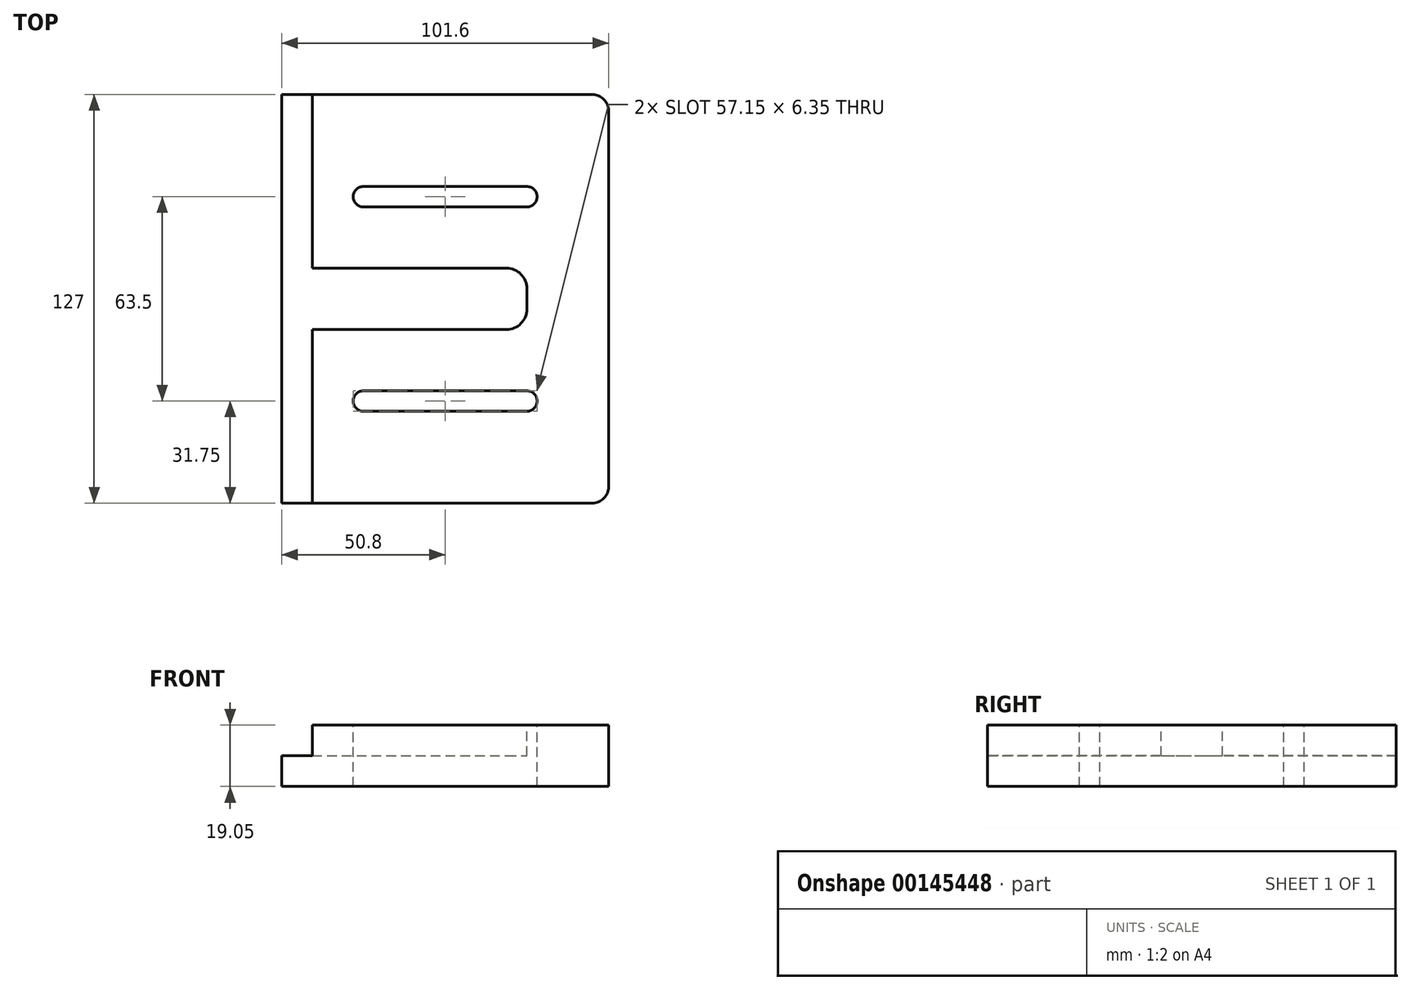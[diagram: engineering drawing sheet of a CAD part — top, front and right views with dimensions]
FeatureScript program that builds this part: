
annotation { "Feature Type Name" : "Feature", "Feature Type Description" : "" }
export const myFeature = defineFeature(function(context is Context, id is Id, definition is map)
    precondition{}
    {
        {
            var Q0;
            Q0=qCreatedBy(makeId("Top.planeOp"),FACE);
            var sketch = newSketch(context, id + "F0", { "sketchPlane" : qUnion([Q0])});
            skLineSegment(sketch, "E0.bottom", {"start": v(0, 0) * mm, "end": v(101.6, 0) * mm});
            skLineSegment(sketch, "E0.top", {"start": v(0, 127) * mm, "end": v(101.6, 127) * mm});
            skLineSegment(sketch, "E0.left", {"start": v(0, 0) * mm, "end": v(0, 127) * mm});
            skLineSegment(sketch, "E0.right", {"start": v(101.6, 0) * mm, "end": v(101.6, 127) * mm});
            skSolve(sketch);
        }
        {
            var Q0;
            Q0=makeQuery(id+"F0.imprint","IMPRINT",FACE,{"disambiguationData":[TD([[makeQuery(id+"F0.imprint","IMPRINT",EDGE,{"derivedFrom":sQuery(id+"F0.wireOp",EDGE,"E0.bottom")}),1.0]])]});
            extrude(context, id + "F1", {"entities" : qUnion([Q0]), "depth" : 19.05 * mm});
        }
        {
            var Q0;
            Q0=makeQuery(id+"F1.opExtrude","CAP_FACE",FACE,{"disambiguationData":[OSD([sQuery(id+"F0.wireOp",EDGE,"E0.bottom"),sQuery(id+"F0.wireOp",EDGE,"E0.top"),sQuery(id+"F0.wireOp",EDGE,"E0.left"),sQuery(id+"F0.wireOp",EDGE,"E0.right")])],"isStart":false});
            var sketch = newSketch(context, id + "F2", { "sketchPlane" : qUnion([Q0])});
            skLineSegment(sketch, "E1.bottom", {"start": v(0, 53.97) * mm, "end": v(76.2, 53.97) * mm});
            skLineSegment(sketch, "E1.top", {"start": v(0, 73.03) * mm, "end": v(76.2, 73.03) * mm});
            skLineSegment(sketch, "E1.left", {"start": v(0, 53.97) * mm, "end": v(0, 73.02) * mm});
            skLineSegment(sketch, "E1.right", {"start": v(76.2, 53.98) * mm, "end": v(76.2, 73.02) * mm});
            skLineSegment(sketch, "E2", {"start": v(76.2, 63.5) * mm, "end": v(0, 63.5) * mm, "construction": true});
            skSolve(sketch);
        }
        {
            var Q0;
            Q0 = qSketchRegion(id + "F2", true);
            extrude(context, id + "F3", {"entities" : qUnion([Q0]), "operationType" : NewBodyOperationType.REMOVE, "oppositeDirection" : true, "depth" : 9.52 * mm});
        }
        {
            var Q0;
            Q0=makeQuery(id+"F3.boolean.opBoolean","COPY",EDGE,{"derivedFrom":makeQuery(id+"F3.opExtrude","SWEPT_EDGE",EDGE,{"disambiguationData":[OSD([sQuery(id+"F2.wireOp",EDGE,"E1.top"),sQuery(id+"F2.wireOp",EDGE,"E1.right")])]})});
            var Q1;
            Q1=makeQuery(id+"F3.boolean.opBoolean","COPY",EDGE,{"derivedFrom":makeQuery(id+"F3.opExtrude","SWEPT_EDGE",EDGE,{"disambiguationData":[OSD([sQuery(id+"F2.wireOp",EDGE,"E1.bottom"),sQuery(id+"F2.wireOp",EDGE,"E1.right")])]})});
            fillet(context, id + "F4", {"entities" : qUnion([Q0, Q1]), "radius" : 6.35 * mm, "tangentPropagation" : true, "allowEdgeOverflow" : false});
        }
        {
            var Q0;
            Q0=makeQuery(id+"F1.opExtrude","CAP_FACE",FACE,{"disambiguationData":[OSD([sQuery(id+"F0.wireOp",EDGE,"E0.bottom"),sQuery(id+"F0.wireOp",EDGE,"E0.top"),sQuery(id+"F0.wireOp",EDGE,"E0.left"),sQuery(id+"F0.wireOp",EDGE,"E0.right")])],"isStart":false});
            var sketch = newSketch(context, id + "F5", { "sketchPlane" : qUnion([Q0])});
            skLineSegment(sketch, "E3", {"start": v(101.6, 63.5) * mm, "end": v(0, 63.5) * mm, "construction": true});
            skLineSegment(sketch, "E4", {"start": v(50.8, 63.5) * mm, "end": v(50.8, 0) * mm, "construction": true});
            skLineSegment(sketch, "E5", {"start": v(25.4, 31.75) * mm, "end": v(76.2, 31.75) * mm});
            skPoint(sketch, "E5.startSnap0", {"position": v(50.8, 31.75) * mm});
            skLineSegment(sketch, "E6.MirrorCS", {"start": v(25.4, 95.25) * mm, "end": v(76.2, 95.25) * mm});
            skArc(sketch, "E7.0.startCap", {"start": v(25.4, 28.58) * mm, "mid": v(22.22, 31.75) * mm, "end": v(25.4, 34.93) * mm});
            skArc(sketch, "E7.0.endCap", {"start": v(76.2, 34.93) * mm, "mid": v(79.37, 31.75) * mm, "end": v(76.2, 28.58) * mm});
            skLineSegment(sketch, "E7.0.left", {"start": v(25.4, 34.93) * mm, "end": v(76.2, 34.93) * mm});
            skLineSegment(sketch, "E7.0.right", {"start": v(25.4, 28.58) * mm, "end": v(76.2, 28.58) * mm});
            skArc(sketch, "E8.0.startCap", {"start": v(25.4, 92.08) * mm, "mid": v(22.23, 95.25) * mm, "end": v(25.4, 98.43) * mm});
            skArc(sketch, "E8.0.endCap", {"start": v(76.2, 98.43) * mm, "mid": v(79.37, 95.25) * mm, "end": v(76.2, 92.08) * mm});
            skLineSegment(sketch, "E8.0.left", {"start": v(25.4, 98.43) * mm, "end": v(76.2, 98.43) * mm});
            skLineSegment(sketch, "E8.0.right", {"start": v(25.4, 92.08) * mm, "end": v(76.2, 92.08) * mm});
            skSolve(sketch);
        }
        {
            var Q0;
            Q0 = qSketchRegion(id + "F5", true);
            extrude(context, id + "F6", {"entities" : qUnion([Q0]), "operationType" : NewBodyOperationType.REMOVE, "endBound" : BoundingType.THROUGH_ALL, "oppositeDirection" : true, "depth" : 25.4 * mm});
        }
        {
            var Q0;
            Q0=makeQuery(id+"F1.opExtrude","SWEPT_EDGE",EDGE,{"disambiguationData":[OSD([sQuery(id+"F0.wireOp",EDGE,"E0.bottom"),sQuery(id+"F0.wireOp",EDGE,"E0.right")])]});
            var Q1;
            Q1=makeQuery(id+"F1.opExtrude","SWEPT_EDGE",EDGE,{"disambiguationData":[OSD([sQuery(id+"F0.wireOp",EDGE,"E0.top"),sQuery(id+"F0.wireOp",EDGE,"E0.right")])]});
            fillet(context, id + "F7", {"entities" : qUnion([Q0, Q1]), "radius" : 5.08 * mm, "tangentPropagation" : true, "allowEdgeOverflow" : false});
        }
        {
            var Q0;
            Q0=makeQuery(id+"F1.opExtrude","SWEPT_FACE",FACE,{"disambiguationData":[OSD([sQuery(id+"F0.wireOp",EDGE,"E0.bottom")])]});
            var sketch = newSketch(context, id + "F8", { "sketchPlane" : qUnion([Q0])});
            skPoint(sketch, "E9.firstSnap0", {"position": v(0, 9.53) * mm});
            skLineSegment(sketch, "E9.bottom", {"start": v(9.53, 9.53) * mm, "end": v(-15.88, 9.53) * mm});
            skLineSegment(sketch, "E9.top", {"start": v(9.52, 28.58) * mm, "end": v(-15.88, 28.58) * mm});
            skLineSegment(sketch, "E9.left", {"start": v(9.53, 9.53) * mm, "end": v(9.52, 28.58) * mm});
            skLineSegment(sketch, "E9.right", {"start": v(-15.88, 9.53) * mm, "end": v(-15.88, 28.58) * mm});
            skSolve(sketch);
        }
        {
            var Q0;
            Q0 = qSketchRegion(id + "F8", true);
            extrude(context, id + "F9", {"entities" : qUnion([Q0]), "operationType" : NewBodyOperationType.REMOVE, "endBound" : BoundingType.THROUGH_ALL, "oppositeDirection" : true, "depth" : 25.4 * mm});
        }
    });
